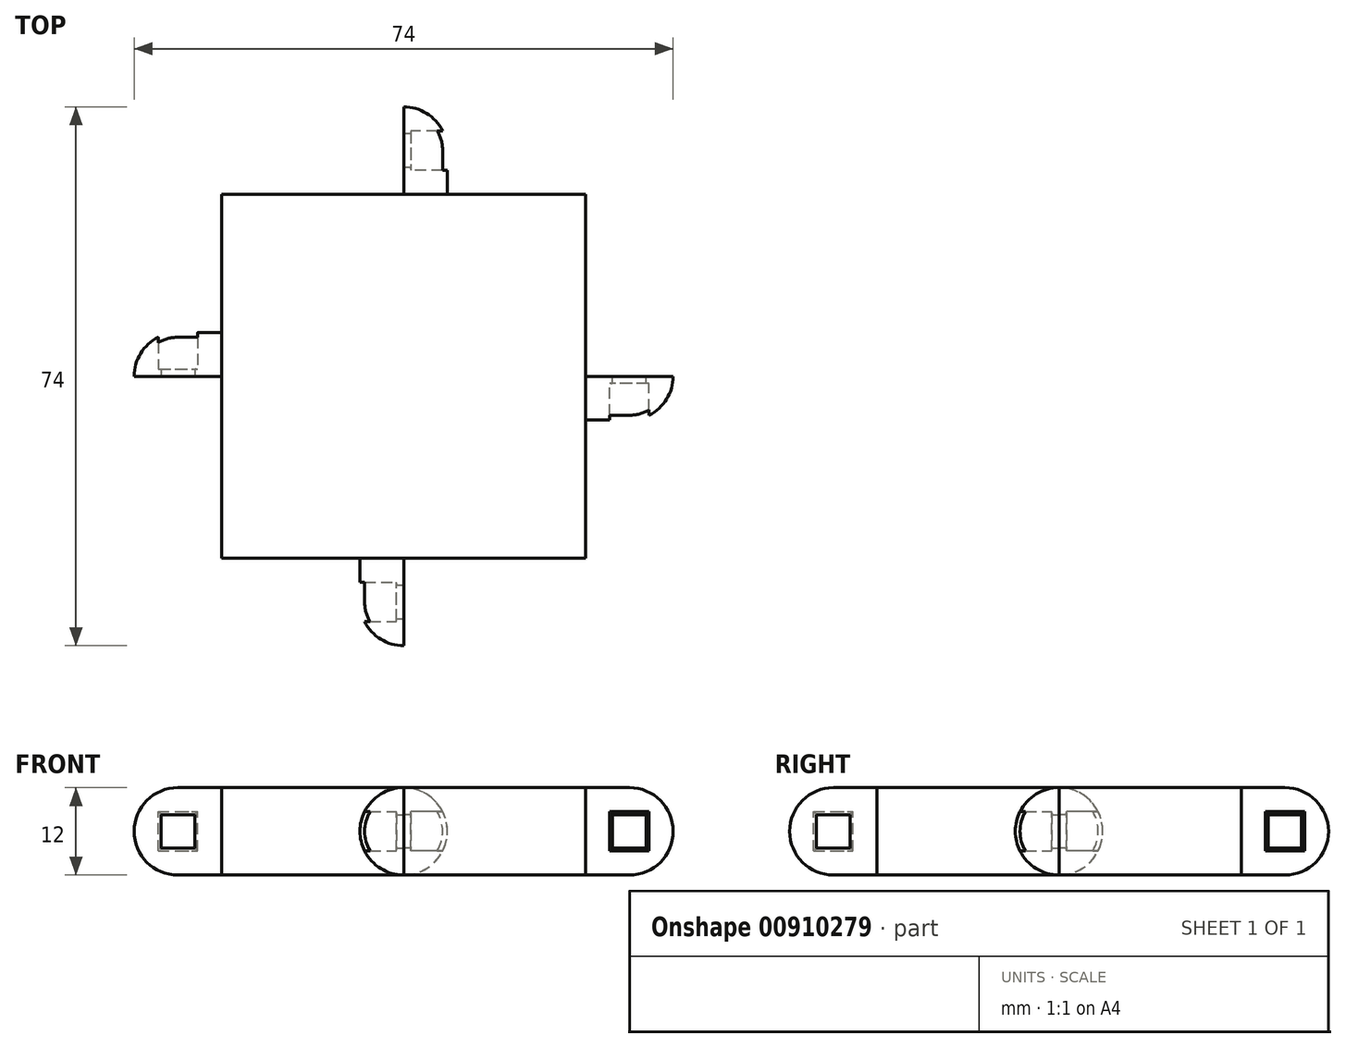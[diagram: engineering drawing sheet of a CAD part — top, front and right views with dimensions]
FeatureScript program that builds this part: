
annotation { "Feature Type Name" : "Feature", "Feature Type Description" : "" }
export const myFeature = defineFeature(function(context is Context, id is Id, definition is map)
    precondition{}
    {
        {
            var Q0;
            Q0=qCreatedBy(makeId("Top.planeOp"),FACE);
            var sketch = newSketch(context, id + "F0", { "sketchPlane" : qUnion([Q0])});
            skLineSegment(sketch, "E0.bottom", {"start": v(-25, 25) * mm, "end": v(25, 25) * mm});
            skLineSegment(sketch, "E0.top", {"start": v(-25, -25) * mm, "end": v(25, -25) * mm});
            skLineSegment(sketch, "E0.left", {"start": v(-25, 25) * mm, "end": v(-25, -25) * mm});
            skLineSegment(sketch, "E0.right", {"start": v(25, 25) * mm, "end": v(25, -25) * mm});
            skSolve(sketch);
        }
        {
            var Q0;
            Q0=makeQuery(id+"F0.imprint","IMPRINT",FACE,{"disambiguationData":[TD([[makeQuery(id+"F0.imprint","IMPRINT",EDGE,{"derivedFrom":sQuery(id+"F0.wireOp",EDGE,"E0.bottom")}),-1.0]])]});
            extrude(context, id + "F1", {"entities" : qUnion([Q0]), "depth" : 12 * mm, "offsetDistance" : 25 * mm});
        }
        {
            var Q0;
            Q0=makeQuery(id+"F1.opExtrude","SWEPT_FACE",FACE,{"disambiguationData":[OSD([sQuery(id+"F0.wireOp",EDGE,"E0.left")])]});
            var sketch = newSketch(context, id + "F2", { "sketchPlane" : qUnion([Q0])});
            skCircle(sketch, "E1", {"center": v(0, 6) * mm, "radius": 6 * mm});
            skSolve(sketch);
        }
        {
            var Q0;
            {var subQ0=sQuery(id+"F2.wireOp",EDGE,"E1");var subQ1=sQuery(id+"F0.wireOp",EDGE,"E0.left");var subQ2=makeQuery(id+"F2.imprint","INTERSECT",VERTEX,{"derivedFrom":[makeQuery(id+"F1.opExtrude","CAP_EDGE",EDGE,{"disambiguationData":[OSD([subQ1])],"isStart":true}),subQ0]});Q0=makeQuery(id+"F2.imprint","IMPRINT",FACE,{"disambiguationData":[TD([[makeQuery(id+"F2.imprint","IMPRINT",EDGE,{"disambiguationData":[TD([[subQ2,1.0]])],"derivedFrom":subQ0}),1.0]])]});}
            extrude(context, id + "F3", {"entities" : qUnion([Q0]), "operationType" : NewBodyOperationType.ADD, "depth" : 12 * mm, "offsetDistance" : 25 * mm});
        }
        {
            var Q0;
            Q0=makeQuery(id+"F3.opExtrude","CAP_EDGE",EDGE,{"disambiguationData":[OSD([sQuery(id+"F2.wireOp",EDGE,"E1")])],"isStart":false});
            fillet(context, id + "F4", {"entities" : qUnion([Q0]), "radius" : 6 * mm, "tangentPropagation" : true, "allowEdgeOverflow" : false});
        }
        {
            var Q0;
            {var subQ0=sQuery(id+"F0.wireOp",EDGE,"E0.left");var subQ1=makeQuery(id+"F1.opExtrude","SWEPT_FACE",FACE,{"disambiguationData":[OSD([subQ0])]});var subQ2=sQuery(id+"F0.wireOp",EDGE,"E0.top");Q0=makeQuery(id+"F3.boolean.opBoolean","SPLIT",FACE,{"disambiguationData":[TD([makeQuery(id+"F1.opExtrude","SWEPT_FACE",FACE,{"disambiguationData":[OSD([subQ2])]})])],"derivedFrom":subQ1});}
            var sketch = newSketch(context, id + "F5", { "sketchPlane" : qUnion([Q0])});
            skLineSegment(sketch, "E2.bottom", {"start": v(0, 12) * mm, "end": v(7.2, 12) * mm});
            skLineSegment(sketch, "E2.top", {"start": v(0, 0) * mm, "end": v(7.2, 0) * mm});
            skLineSegment(sketch, "E2.left", {"start": v(0, 12) * mm, "end": v(0, 0) * mm});
            skLineSegment(sketch, "E2.right", {"start": v(7.2, 12) * mm, "end": v(7.2, 0) * mm});
            skSolve(sketch);
        }
        {
            var Q0;
            Q0 = qSketchRegion(id + "F5", true);
            extrude(context, id + "F6", {"entities" : qUnion([Q0]), "operationType" : NewBodyOperationType.REMOVE, "depth" : 25 * mm, "offsetDistance" : 25 * mm});
        }
        {
            var Q0;
            Q0=makeQuery(id+"F6.boolean.opBoolean","COPY",FACE,{"derivedFrom":makeQuery(id+"F6.opExtrude","SWEPT_FACE",FACE,{"disambiguationData":[OSD([sQuery(id+"F5.wireOp",EDGE,"E2.left")])]})});
            var sketch = newSketch(context, id + "F7", { "sketchPlane" : qUnion([Q0])});
            skLineSegment(sketch, "E3.bottom", {"start": v(-33.7, 3.3) * mm, "end": v(-28.3, 3.3) * mm});
            skLineSegment(sketch, "E3.top", {"start": v(-33.7, 8.7) * mm, "end": v(-28.3, 8.7) * mm});
            skLineSegment(sketch, "E3.left", {"start": v(-33.7, 3.3) * mm, "end": v(-33.7, 8.7) * mm});
            skLineSegment(sketch, "E3.right", {"start": v(-28.3, 3.3) * mm, "end": v(-28.3, 8.7) * mm});
            skSolve(sketch);
        }
        {
            var Q0;
            Q0=makeQuery(id+"F7.imprint","IMPRINT",FACE,{"disambiguationData":[TD([[makeQuery(id+"F7.imprint","IMPRINT",EDGE,{"derivedFrom":sQuery(id+"F7.wireOp",EDGE,"E3.bottom")}),1.0]])]});
            extrude(context, id + "F8", {"entities" : qUnion([Q0]), "operationType" : NewBodyOperationType.REMOVE, "oppositeDirection" : true, "depth" : 25 * mm, "offsetDistance" : 25 * mm});
        }
        {
            var Q0;
            Q0=makeQuery(id+"F6.boolean.opBoolean","COPY",FACE,{"derivedFrom":makeQuery(id+"F6.opExtrude","SWEPT_FACE",FACE,{"disambiguationData":[OSD([sQuery(id+"F5.wireOp",EDGE,"E2.left")])]})});
            var sketch = newSketch(context, id + "F9", { "sketchPlane" : qUnion([Q0])});
            skLineSegment(sketch, "E4.bottom", {"start": v(-34.34, 9.58) * mm, "end": v(-27.42, 9.58) * mm});
            skLineSegment(sketch, "E4.top", {"start": v(-34.34, 2.54) * mm, "end": v(-27.42, 2.54) * mm});
            skLineSegment(sketch, "E4.left", {"start": v(-34.34, 9.58) * mm, "end": v(-34.34, 2.54) * mm});
            skLineSegment(sketch, "E4.right", {"start": v(-27.42, 9.58) * mm, "end": v(-27.42, 2.54) * mm});
            skLineSegment(sketch, "E5.bottom", {"start": v(-33.3, 8.3) * mm, "end": v(-28.7, 8.3) * mm});
            skLineSegment(sketch, "E5.top", {"start": v(-33.3, 3.7) * mm, "end": v(-28.7, 3.7) * mm});
            skLineSegment(sketch, "E5.left", {"start": v(-33.3, 8.3) * mm, "end": v(-33.3, 3.7) * mm});
            skLineSegment(sketch, "E5.right", {"start": v(-28.7, 8.3) * mm, "end": v(-28.7, 3.7) * mm});
            skSolve(sketch);
        }
        {
            var Q0;
            Q0=makeQuery(id+"F9.imprint","IMPRINT",FACE,{"disambiguationData":[TD([[makeQuery(id+"F9.imprint","IMPRINT",EDGE,{"derivedFrom":sQuery(id+"F9.wireOp",EDGE,"E5.bottom")}),1.0]])]});
            extrude(context, id + "F10", {"entities" : qUnion([Q0]), "operationType" : NewBodyOperationType.ADD, "oppositeDirection" : true, "depth" : 1 * mm, "offsetDistance" : 25 * mm});
        }
        {
            var Q0;
            Q0=makeQuery(id+"F10.opExtrude","CAP_EDGE",EDGE,{"disambiguationData":[OSD([sQuery(id+"F9.wireOp",EDGE,"E5.right")])],"isStart":false});
            var Q1;
            Q1=makeQuery(id+"F10.opExtrude","CAP_EDGE",EDGE,{"disambiguationData":[OSD([sQuery(id+"F7.wireOp",EDGE,"E3.right")])],"isStart":false});
            var Q2;
            Q2=makeQuery(id+"F10.opExtrude","CAP_EDGE",EDGE,{"disambiguationData":[OSD([sQuery(id+"F7.wireOp",EDGE,"E3.top")])],"isStart":false});
            var Q3;
            Q3=makeQuery(id+"F10.opExtrude","CAP_EDGE",EDGE,{"disambiguationData":[OSD([sQuery(id+"F9.wireOp",EDGE,"E5.bottom")])],"isStart":false});
            var Q4;
            Q4=makeQuery(id+"F10.opExtrude","CAP_EDGE",EDGE,{"disambiguationData":[OSD([sQuery(id+"F7.wireOp",EDGE,"E3.left")])],"isStart":false});
            var Q5;
            Q5=makeQuery(id+"F10.opExtrude","CAP_EDGE",EDGE,{"disambiguationData":[OSD([sQuery(id+"F9.wireOp",EDGE,"E5.left")])],"isStart":false});
            var Q6;
            Q6=makeQuery(id+"F10.opExtrude","CAP_EDGE",EDGE,{"disambiguationData":[OSD([sQuery(id+"F7.wireOp",EDGE,"E3.bottom")])],"isStart":false});
            var Q7;
            Q7=makeQuery(id+"F10.opExtrude","CAP_EDGE",EDGE,{"disambiguationData":[OSD([sQuery(id+"F9.wireOp",EDGE,"E5.top")])],"isStart":false});
            fillet(context, id + "F11", {"entities" : qUnion([Q0, Q1, Q2, Q3, Q4, Q5, Q6, Q7]), "radius" : 0.2 * mm, "tangentPropagation" : true, "allowEdgeOverflow" : false});
        }
        {
            var Q0;
            Q0=qCreatedBy(makeId("Right.planeOp"),FACE);
            var sketch = newSketch(context, id + "F12", { "sketchPlane" : qUnion([Q0])});
            skLineSegment(sketch, "E6", {"start": v(0, 0) * mm, "end": v(0, 27.3) * mm});
            skSolve(sketch);
        }
        {
            var Q0;
            {var subQ0=sQuery(id+"F0.wireOp",EDGE,"E0.left");var subQ1=makeQuery(id+"F1.opExtrude","SWEPT_FACE",FACE,{"disambiguationData":[OSD([subQ0])]});var subQ2=sQuery(id+"F0.wireOp",EDGE,"E0.top");Q0=makeQuery(id+"F6.boolean.opBoolean","MERGE",FACE,{"derivedFrom":[makeQuery(id+"F3.boolean.opBoolean","SPLIT",FACE,{"disambiguationData":[TD([makeQuery(id+"F1.opExtrude","SWEPT_FACE",FACE,{"disambiguationData":[OSD([subQ2])]})])],"derivedFrom":subQ1})],"fromTools":[makeQuery(id+"F6.opExtrude","CAP_FACE",FACE,{"disambiguationData":[OSD([sQuery(id+"F5.wireOp",EDGE,"E2.bottom"),sQuery(id+"F5.wireOp",EDGE,"E2.top"),sQuery(id+"F5.wireOp",EDGE,"E2.left"),sQuery(id+"F5.wireOp",EDGE,"E2.right")])],"isStart":true})]});}
            var sketch = newSketch(context, id + "F13", { "sketchPlane" : qUnion([Q0])});
            skLineSegment(sketch, "E7.bottom", {"start": v(0, 0) * mm, "end": v(25, 0) * mm});
            skLineSegment(sketch, "E7.top", {"start": v(0, 12) * mm, "end": v(25, 12) * mm});
            skLineSegment(sketch, "E7.left", {"start": v(0, 0) * mm, "end": v(0, 12) * mm});
            skLineSegment(sketch, "E7.right", {"start": v(25, 0) * mm, "end": v(25, 12) * mm});
            skSolve(sketch);
        }
        {
            var Q0;
            Q0=makeQuery(id+"F13.imprint","IMPRINT",FACE,{"disambiguationData":[TD([[makeQuery(id+"F13.imprint","IMPRINT",EDGE,{"derivedFrom":sQuery(id+"F13.wireOp",EDGE,"E7.bottom")}),1.0]])]});
            extrude(context, id + "F14", {"entities" : qUnion([Q0]), "operationType" : NewBodyOperationType.REMOVE, "oppositeDirection" : true, "depth" : 50 * mm, "offsetDistance" : 25 * mm});
        }
        {
            var Q0;
            Q0=makeQuery(id+"F1.opExtrude","SWEPT_FACE",FACE,{"disambiguationData":[OSD([sQuery(id+"F0.wireOp",EDGE,"E0.bottom")])]});
            var sketch = newSketch(context, id + "F15", { "sketchPlane" : qUnion([Q0])});
            skLineSegment(sketch, "E8.bottom", {"start": v(-25, 12) * mm, "end": v(0, 12) * mm});
            skLineSegment(sketch, "E8.top", {"start": v(-25, 0) * mm, "end": v(0, 0) * mm});
            skLineSegment(sketch, "E8.left", {"start": v(-25, 12) * mm, "end": v(-25, 0) * mm});
            skLineSegment(sketch, "E8.right", {"start": v(0, 12) * mm, "end": v(0, 0) * mm});
            skSolve(sketch);
        }
        {
            var Q0;
            Q0=makeQuery(id+"F15.imprint","IMPRINT",FACE,{"disambiguationData":[TD([[makeQuery(id+"F15.imprint","IMPRINT",EDGE,{"derivedFrom":sQuery(id+"F15.wireOp",EDGE,"E8.bottom")}),1.0]])]});
            extrude(context, id + "F16", {"entities" : qUnion([Q0]), "operationType" : NewBodyOperationType.REMOVE, "oppositeDirection" : true, "depth" : 25 * mm, "offsetDistance" : 25 * mm});
        }
        {
            var Q0;
            Q0=makeQuery(id+"F1.opExtrude","SWEPT_BODY",BODY,{"disambiguationData":[OSD([sQuery(id+"F0.wireOp",EDGE,"E0.bottom"),sQuery(id+"F0.wireOp",EDGE,"E0.top"),sQuery(id+"F0.wireOp",EDGE,"E0.left"),sQuery(id+"F0.wireOp",EDGE,"E0.right")])]});
            var Q1;
            Q1=sQuery(id+"F12.wireOp",EDGE,"E6");
            circularPattern(context, id + "F17", {"operationType" : NewBodyOperationType.ADD, "entities" : qUnion([Q0]), "axis" : qUnion([Q1]), "angle" : 360 * degree, "instanceCount" : 4, "equalSpace" : true});
        }
    });
